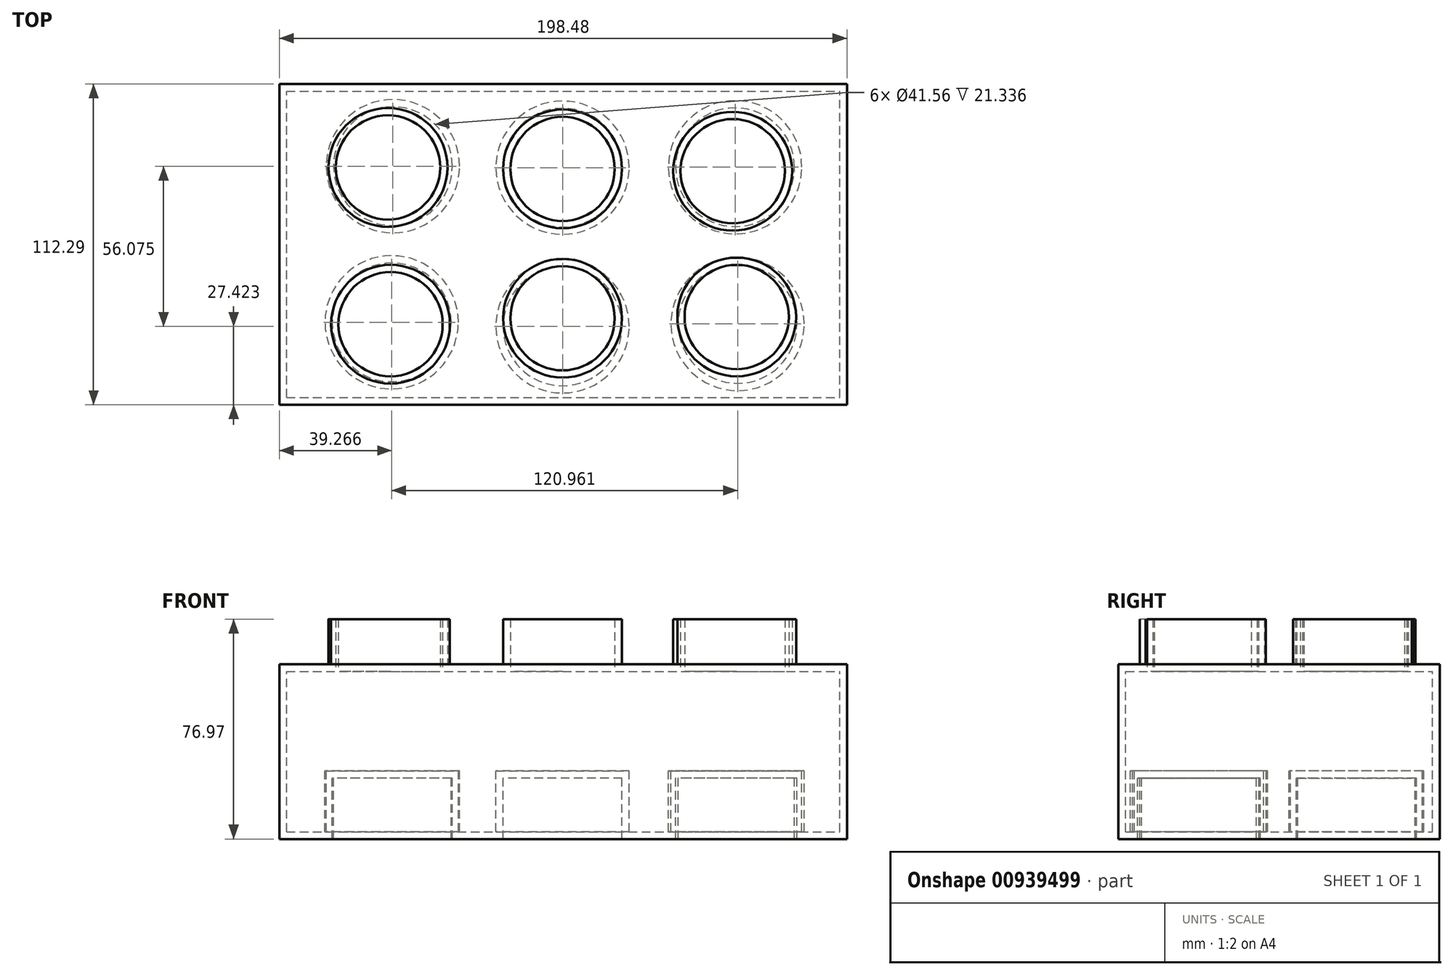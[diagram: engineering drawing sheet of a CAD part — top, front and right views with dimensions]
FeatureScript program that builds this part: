
annotation { "Feature Type Name" : "Feature", "Feature Type Description" : "" }
export const myFeature = defineFeature(function(context is Context, id is Id, definition is map)
    precondition{}
    {
        {
            var Q0;
            Q0=qCreatedBy(makeId("Top.planeOp"),FACE);
            var sketch = newSketch(context, id + "F0", { "sketchPlane" : qUnion([Q0])});
            skLineSegment(sketch, "E0.bottom", {"start": v(-99.02, 55.45) * mm, "end": v(99.46, 55.45) * mm});
            skLineSegment(sketch, "E0.top", {"start": v(-99.02, -56.85) * mm, "end": v(99.46, -56.85) * mm});
            skLineSegment(sketch, "E0.left", {"start": v(-99.02, 55.45) * mm, "end": v(-99.02, -56.85) * mm});
            skLineSegment(sketch, "E0.right", {"start": v(99.46, 55.45) * mm, "end": v(99.46, -56.85) * mm});
            skSolve(sketch);
        }
        {
            var Q0;
            Q0=makeQuery(id+"F0.imprint","IMPRINT",FACE,{"disambiguationData":[TD([[makeQuery(id+"F0.imprint","IMPRINT",EDGE,{"derivedFrom":sQuery(id+"F0.wireOp",EDGE,"E0.bottom")}),-1.0]])]});
            extrude(context, id + "F1", {"entities" : qUnion([Q0]), "depth" : 39.88 * mm, "offsetDistance" : 25.4 * mm});
        }
        {
            var Q0;
            Q0=makeQuery(id+"F1.opExtrude","CAP_FACE",FACE,{"disambiguationData":[OSD([sQuery(id+"F0.wireOp",EDGE,"E0.bottom"),sQuery(id+"F0.wireOp",EDGE,"E0.top"),sQuery(id+"F0.wireOp",EDGE,"E0.left"),sQuery(id+"F0.wireOp",EDGE,"E0.right")])],"isStart":true});
            var sketch = newSketch(context, id + "F2", { "sketchPlane" : qUnion([Q0])});
            skCircle(sketch, "E1", {"center": v(0, 27.1) * mm, "radius": 20.78 * mm});
            skCircle(sketch, "E2", {"center": v(0, -25.18) * mm, "radius": 20.78 * mm});
            skCircle(sketch, "E3", {"center": v(-61.04, 27.62) * mm, "radius": 20.78 * mm});
            skCircle(sketch, "E4", {"center": v(-60.16, -27.25) * mm, "radius": 20.78 * mm});
            skCircle(sketch, "E5", {"center": v(59.5, 26.3) * mm, "radius": 20.78 * mm});
            skCircle(sketch, "E6", {"center": v(60.9, -24.72) * mm, "radius": 20.78 * mm});
            skSolve(sketch);
        }
        {
            var Q0;
            Q0=makeQuery(id+"F2.imprint","IMPRINT",FACE,{"disambiguationData":[TD([[makeQuery(id+"F2.imprint","IMPRINT",EDGE,{"derivedFrom":sQuery(id+"F2.wireOp",EDGE,"E3")}),1.0]])]});
            var Q1;
            Q1=makeQuery(id+"F2.imprint","IMPRINT",FACE,{"disambiguationData":[TD([[makeQuery(id+"F2.imprint","IMPRINT",EDGE,{"derivedFrom":sQuery(id+"F2.wireOp",EDGE,"E4")}),1.0]])]});
            var Q2;
            Q2=makeQuery(id+"F2.imprint","IMPRINT",FACE,{"disambiguationData":[TD([[makeQuery(id+"F2.imprint","IMPRINT",EDGE,{"derivedFrom":sQuery(id+"F2.wireOp",EDGE,"E2")}),1.0]])]});
            var Q3;
            Q3=makeQuery(id+"F2.imprint","IMPRINT",FACE,{"disambiguationData":[TD([[makeQuery(id+"F2.imprint","IMPRINT",EDGE,{"derivedFrom":sQuery(id+"F2.wireOp",EDGE,"E1")}),1.0]])]});
            var Q4;
            Q4=makeQuery(id+"F2.imprint","IMPRINT",FACE,{"disambiguationData":[TD([[makeQuery(id+"F2.imprint","IMPRINT",EDGE,{"derivedFrom":sQuery(id+"F2.wireOp",EDGE,"E6")}),1.0]])]});
            var Q5;
            Q5=makeQuery(id+"F2.imprint","IMPRINT",FACE,{"disambiguationData":[TD([[makeQuery(id+"F2.imprint","IMPRINT",EDGE,{"derivedFrom":sQuery(id+"F2.wireOp",EDGE,"E5")}),1.0]])]});
            extrude(context, id + "F3", {"entities" : qUnion([Q0, Q1, Q2, Q3, Q4, Q5]), "operationType" : NewBodyOperationType.ADD, "depth" : 15.75 * mm, "offsetDistance" : 25.4 * mm});
        }
        {
            var Q0;
            Q0=makeQuery(id+"F1.opExtrude","CAP_FACE",FACE,{"disambiguationData":[OSD([sQuery(id+"F0.wireOp",EDGE,"E0.bottom"),sQuery(id+"F0.wireOp",EDGE,"E0.top"),sQuery(id+"F0.wireOp",EDGE,"E0.left"),sQuery(id+"F0.wireOp",EDGE,"E0.right")])],"isStart":false});
            var sketch = newSketch(context, id + "F4", { "sketchPlane" : qUnion([Q0])});
            skCircle(sketch, "E7", {"center": v(0, 28.02) * mm, "radius": 20.78 * mm});
            skCircle(sketch, "E8", {"center": v(0, -27.54) * mm, "radius": 20.78 * mm});
            skCircle(sketch, "E9", {"center": v(-59.75, 26.6) * mm, "radius": 20.78 * mm});
            skCircle(sketch, "E10", {"center": v(-59.32, -28.06) * mm, "radius": 20.78 * mm});
            skCircle(sketch, "E11", {"center": v(61.2, 27.18) * mm, "radius": 20.78 * mm});
            skCircle(sketch, "E12", {"center": v(60.35, -27.7) * mm, "radius": 20.78 * mm});
            skSolve(sketch);
        }
        {
            var Q0;
            Q0=makeQuery(id+"F4.imprint","IMPRINT",FACE,{"disambiguationData":[TD([[makeQuery(id+"F4.imprint","IMPRINT",EDGE,{"derivedFrom":sQuery(id+"F4.wireOp",EDGE,"E7")}),-1.0]])]});
            extrude(context, id + "F5", {"entities" : qUnion([Q0]), "operationType" : NewBodyOperationType.ADD, "depth" : 21.34 * mm, "offsetDistance" : 25.4 * mm});
        }
        {
            var Q0;
            Q0=makeQuery(id+"F1.opExtrude","SWEPT_BODY",BODY,{"disambiguationData":[OSD([sQuery(id+"F0.wireOp",EDGE,"E0.bottom"),sQuery(id+"F0.wireOp",EDGE,"E0.top"),sQuery(id+"F0.wireOp",EDGE,"E0.left"),sQuery(id+"F0.wireOp",EDGE,"E0.right")])]});
            var Q1;
            Q1=makeQuery(id+"F5.opExtrude","CAP_EDGE",EDGE,{"disambiguationData":[OSD([sQuery(id+"F0.wireOp",EDGE,"E0.top")])],"isStart":false});
            transform(context, id + "F6", {"entities" : qUnion([Q0]), "transformType" : TransformType.ROTATION, "transformAxis" : qUnion([Q1]), "angle" : 180 * degree, "makeCopy" : false});
        }
        {
            var Q0;
            Q0=makeQuery(id+"F3.opExtrude","CAP_FACE",FACE,{"disambiguationData":[OSD([sQuery(id+"F2.wireOp",EDGE,"E4")])],"isStart":false});
            var Q1;
            Q1=makeQuery(id+"F3.opExtrude","CAP_FACE",FACE,{"disambiguationData":[OSD([sQuery(id+"F2.wireOp",EDGE,"E3")])],"isStart":false});
            var Q2;
            Q2=makeQuery(id+"F3.opExtrude","CAP_FACE",FACE,{"disambiguationData":[OSD([sQuery(id+"F2.wireOp",EDGE,"E1")])],"isStart":false});
            var Q3;
            Q3=makeQuery(id+"F3.opExtrude","CAP_FACE",FACE,{"disambiguationData":[OSD([sQuery(id+"F2.wireOp",EDGE,"E2")])],"isStart":false});
            var Q4;
            Q4=makeQuery(id+"F3.opExtrude","CAP_FACE",FACE,{"disambiguationData":[OSD([sQuery(id+"F2.wireOp",EDGE,"E6")])],"isStart":false});
            var Q5;
            Q5=makeQuery(id+"F3.opExtrude","CAP_FACE",FACE,{"disambiguationData":[OSD([sQuery(id+"F2.wireOp",EDGE,"E5")])],"isStart":false});
            shell(context, id + "F7", {"entities" : qUnion([Q0, Q1, Q2, Q3, Q4, Q5]), "thickness" : 2.54 * mm});
        }
    });
